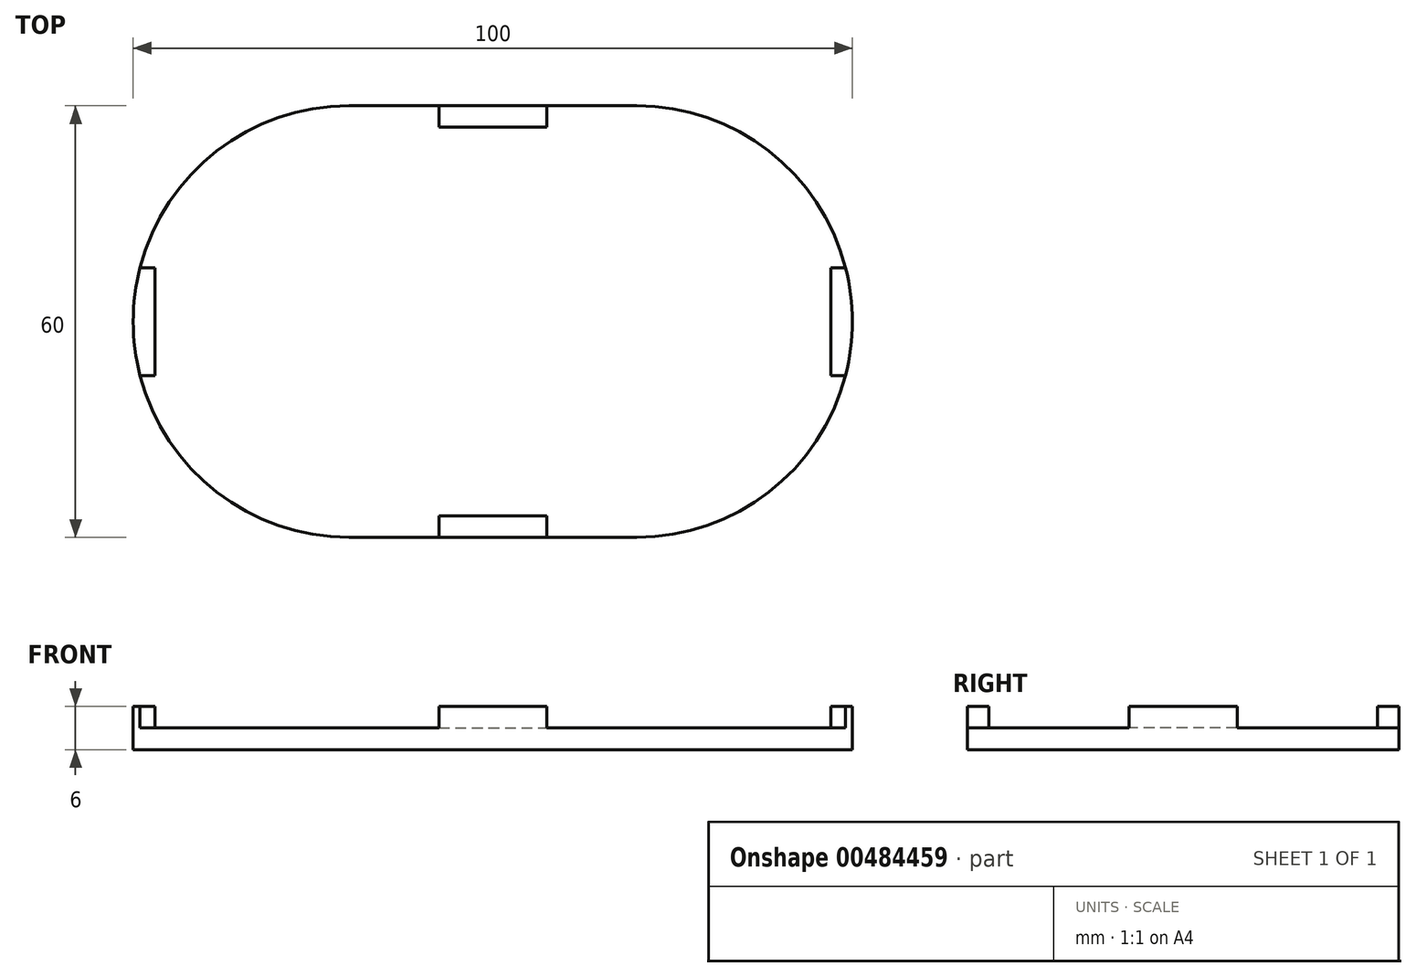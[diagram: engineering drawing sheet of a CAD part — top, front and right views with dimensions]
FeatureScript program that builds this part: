
annotation { "Feature Type Name" : "Feature", "Feature Type Description" : "" }
export const myFeature = defineFeature(function(context is Context, id is Id, definition is map)
    precondition{}
    {
        {
            var Q0;
            Q0=qCreatedBy(makeId("Top.planeOp"),FACE);
            var sketch = newSketch(context, id + "F0", { "sketchPlane" : qUnion([Q0])});
            skLineSegment(sketch, "E0.bottom", {"start": v(-20, 30) * mm, "end": v(20, 30) * mm});
            skLineSegment(sketch, "E0.top", {"start": v(-20, -30) * mm, "end": v(20, -30) * mm});
            skLineSegment(sketch, "E0.left", {"start": v(-50, 0) * mm, "end": v(-50, 0) * mm});
            skLineSegment(sketch, "E0.right", {"start": v(50, 0) * mm, "end": v(50, 0) * mm});
            skPoint(sketch, "E1.visualSharp", {"position": v(-50, 30) * mm});
            skArc(sketch, "E1.filletArc", {"start": v(-20, 30) * mm, "mid": v(-41.21, 21.21) * mm, "end": v(-50, 0) * mm});
            skPoint(sketch, "E2.visualSharp", {"position": v(-50, -30) * mm});
            skArc(sketch, "E2.filletArc", {"start": v(-50, 0) * mm, "mid": v(-41.21, -21.21) * mm, "end": v(-20, -30) * mm});
            skPoint(sketch, "E3.visualSharp", {"position": v(50, -30) * mm});
            skArc(sketch, "E3.filletArc", {"start": v(20, -30) * mm, "mid": v(41.21, -21.21) * mm, "end": v(50, 0) * mm});
            skPoint(sketch, "E4.visualSharp", {"position": v(50, 30) * mm});
            skArc(sketch, "E4.filletArc", {"start": v(50, 0) * mm, "mid": v(41.21, 21.21) * mm, "end": v(20, 30) * mm});
            skSolve(sketch);
        }
        {
            var Q0;
            Q0=makeQuery(id+"F0.imprint","IMPRINT",FACE,{"disambiguationData":[TD([[makeQuery(id+"F0.imprint","IMPRINT",EDGE,{"derivedFrom":sQuery(id+"F0.wireOp",EDGE,"E0.bottom")}),-1.0]])]});
            extrude(context, id + "F1", {"entities" : qUnion([Q0]), "depth" : 3 * mm});
        }
        {
            var Q0;
            Q0=makeQuery(id+"F1.opExtrude","CAP_FACE",FACE,{"disambiguationData":[OSD([sQuery(id+"F0.wireOp",EDGE,"E0.bottom"),sQuery(id+"F0.wireOp",EDGE,"E0.top"),sQuery(id+"F0.wireOp",EDGE,"E1.filletArc"),sQuery(id+"F0.wireOp",EDGE,"E2.filletArc"),sQuery(id+"F0.wireOp",EDGE,"E3.filletArc"),sQuery(id+"F0.wireOp",EDGE,"E4.filletArc")])],"isStart":false});
            var sketch = newSketch(context, id + "F2", { "sketchPlane" : qUnion([Q0])});
            skLineSegment(sketch, "E5.bottom", {"start": v(-7.5, 30) * mm, "end": v(7.5, 30) * mm});
            skLineSegment(sketch, "E5.top", {"start": v(-7.5, 27) * mm, "end": v(7.5, 27) * mm});
            skLineSegment(sketch, "E5.left", {"start": v(-7.5, 30) * mm, "end": v(-7.5, 27) * mm});
            skLineSegment(sketch, "E5.right", {"start": v(7.5, 30) * mm, "end": v(7.5, 27) * mm});
            skLineSegment(sketch, "E6.MirrorCS", {"start": v(7.5, -30) * mm, "end": v(7.5, -27) * mm});
            skLineSegment(sketch, "E7.MirrorCS", {"start": v(-7.5, -30) * mm, "end": v(-7.5, -27) * mm});
            skLineSegment(sketch, "E8.MirrorCS", {"start": v(-7.5, -30) * mm, "end": v(7.5, -30) * mm});
            skLineSegment(sketch, "E9.MirrorCS", {"start": v(-7.5, -27) * mm, "end": v(7.5, -27) * mm});
            skLineSegment(sketch, "E10.bottom", {"start": v(-50, 7.5) * mm, "end": v(-47, 7.5) * mm});
            skLineSegment(sketch, "E10.top", {"start": v(-50, -7.5) * mm, "end": v(-47, -7.5) * mm});
            skLineSegment(sketch, "E10.left", {"start": v(-50, 7.5) * mm, "end": v(-50, -7.5) * mm});
            skLineSegment(sketch, "E10.right", {"start": v(-47, 7.5) * mm, "end": v(-47, -7.5) * mm});
            skLineSegment(sketch, "E11.MirrorCS", {"start": v(50, 7.5) * mm, "end": v(47, 7.5) * mm});
            skLineSegment(sketch, "E12.MirrorCS", {"start": v(50, -7.5) * mm, "end": v(47, -7.5) * mm});
            skLineSegment(sketch, "E13.MirrorCS", {"start": v(47, 7.5) * mm, "end": v(47, -7.5) * mm});
            skLineSegment(sketch, "E14.MirrorCS", {"start": v(50, 7.5) * mm, "end": v(50, -7.5) * mm});
            skSolve(sketch);
        }
        {
            var Q0;
            Q0=makeQuery(id+"F2.imprint","IMPRINT",FACE,{"disambiguationData":[TD([[makeQuery(id+"F2.imprint","IMPRINT",EDGE,{"derivedFrom":sQuery(id+"F2.wireOp",EDGE,"E5.bottom")}),-1.0]])]});
            var Q1;
            {var subQ4=sQuery(id+"F2.wireOp",EDGE,"E10.right");Q1=makeQuery(id+"F2.imprint","IMPRINT",FACE,{"disambiguationData":[TD([[makeQuery(id+"F2.imprint","IMPRINT",EDGE,{"derivedFrom":subQ4}),-1.0]])]});}
            var Q2;
            Q2=makeQuery(id+"F2.imprint","IMPRINT",FACE,{"disambiguationData":[TD([[makeQuery(id+"F2.imprint","IMPRINT",EDGE,{"derivedFrom":sQuery(id+"F2.wireOp",EDGE,"E6.MirrorCS")}),1.0]])]});
            var Q3;
            {var subQ4=sQuery(id+"F2.wireOp",EDGE,"E13.MirrorCS");Q3=makeQuery(id+"F2.imprint","IMPRINT",FACE,{"disambiguationData":[TD([[makeQuery(id+"F2.imprint","IMPRINT",EDGE,{"derivedFrom":subQ4}),1.0]])]});}
            extrude(context, id + "F3", {"entities" : qUnion([Q0, Q1, Q2, Q3]), "operationType" : NewBodyOperationType.ADD, "depth" : 3 * mm});
        }
    });
